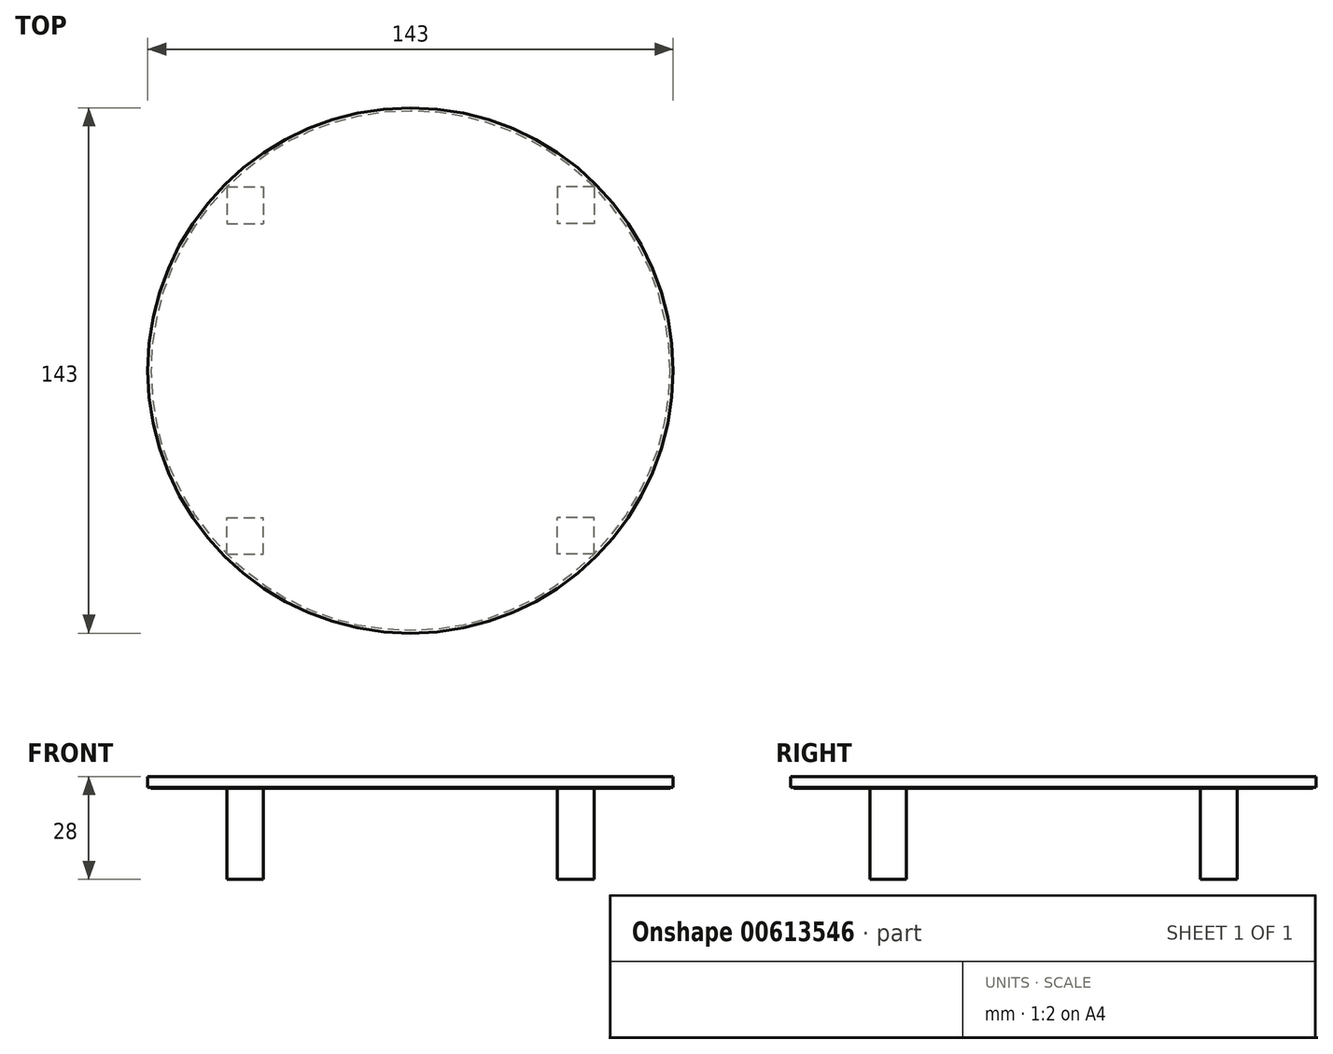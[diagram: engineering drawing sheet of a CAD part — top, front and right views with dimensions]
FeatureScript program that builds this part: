
annotation { "Feature Type Name" : "Feature", "Feature Type Description" : "" }
export const myFeature = defineFeature(function(context is Context, id is Id, definition is map)
    precondition{}
    {
        {
            var Q0;
            Q0=qCreatedBy(makeId("Top.planeOp"),FACE);
            var sketch = newSketch(context, id + "F0", { "sketchPlane" : qUnion([Q0])});
            skLineSegment(sketch, "E0.bottom", {"start": v(50, -50) * mm, "end": v(40, -50) * mm});
            skLineSegment(sketch, "E0.top", {"start": v(50, 50) * mm, "end": v(40, 50) * mm});
            skLineSegment(sketch, "E0.left", {"start": v(50, -50) * mm, "end": v(50, -40) * mm});
            skLineSegment(sketch, "E0.right", {"start": v(-50, -50) * mm, "end": v(-50, -40) * mm});
            skPoint(sketch, "E0.middle", {"position": v(0, 0) * mm});
            skLineSegment(sketch, "E1.bottom", {"start": v(-50, 50) * mm, "end": v(-40, 50) * mm});
            skLineSegment(sketch, "E1.top", {"start": v(-50, 40) * mm, "end": v(-40, 40) * mm});
            skLineSegment(sketch, "E1.left", {"start": v(-50, 50) * mm, "end": v(-50, 40) * mm});
            skLineSegment(sketch, "E1.right", {"start": v(-40, 50) * mm, "end": v(-40, 40) * mm});
            skLineSegment(sketch, "E2.top", {"start": v(50, 40) * mm, "end": v(40, 40) * mm});
            skLineSegment(sketch, "E2.left", {"start": v(50, 50) * mm, "end": v(50, 40) * mm});
            skLineSegment(sketch, "E2.right", {"start": v(40, 50) * mm, "end": v(40, 40) * mm});
            skLineSegment(sketch, "E3.top", {"start": v(50, -40) * mm, "end": v(40, -40) * mm});
            skLineSegment(sketch, "E3.right", {"start": v(40, -50) * mm, "end": v(40, -40) * mm});
            skLineSegment(sketch, "E4.bottom", {"start": v(-50, -50) * mm, "end": v(-40, -50) * mm});
            skLineSegment(sketch, "E4.top", {"start": v(-50, -40) * mm, "end": v(-40, -40) * mm});
            skLineSegment(sketch, "E4.right", {"start": v(-40, -50) * mm, "end": v(-40, -40) * mm});
            skLineSegment(sketch, "E5.trimOffspring", {"start": v(-40, 50) * mm, "end": v(-50, 50) * mm});
            skLineSegment(sketch, "E6.trimOffspring", {"start": v(50, 40) * mm, "end": v(50, 50) * mm});
            skLineSegment(sketch, "E7.trimOffspring", {"start": v(-40, -50) * mm, "end": v(-50, -50) * mm});
            skLineSegment(sketch, "E8.trimOffspring", {"start": v(-50, 40) * mm, "end": v(-50, 50) * mm});
            skSolve(sketch);
        }
        {
            var Q0;
            Q0 = qSketchRegion(id + "F0", true);
            extrude(context, id + "F1", {"entities" : qUnion([Q0]), "depth" : 25 * mm, "offsetDistance" : 25 * mm});
        }
        {
            var Q0;
            Q0=makeQuery(id+"F1.opExtrude","CAP_FACE",FACE,{"disambiguationData":[OSD([sQuery(id+"F0.wireOp",EDGE,"E1.top"),sQuery(id+"F0.wireOp",EDGE,"E1.right"),sQuery(id+"F0.wireOp",EDGE,"E5.trimOffspring"),sQuery(id+"F0.wireOp",EDGE,"E8.trimOffspring")])],"isStart":false});
            var sketch = newSketch(context, id + "F2", { "sketchPlane" : qUnion([Q0])});
            skCircle(sketch, "E9", {"center": v(0, 0) * mm, "radius": 71.5 * mm});
            skSolve(sketch);
        }
        {
            var Q0;
            Q0 = qSketchRegion(id + "F2", true);
            extrude(context, id + "F3", {"entities" : qUnion([Q0]), "depth" : 3 * mm, "offsetDistance" : 25 * mm});
        }
        {
            var Q0;
            Q0=makeQuery(id+"F3.opExtrude","CAP_FACE",FACE,{"disambiguationData":[OSD([sQuery(id+"F2.wireOp",EDGE,"E9")])],"isStart":false});
            var sketch = newSketch(context, id + "F4", { "sketchPlane" : qUnion([Q0])});
            skCircle(sketch, "E10", {"center": v(0, 0) * mm, "radius": 50 * mm});
            skSolve(sketch);
        }
        {
            var Q0;
            Q0=sQuery(id+"F4.wireOp",EDGE,"E10");
            extrude(context, id + "F5", {"bodyType" : ToolBodyType.SURFACE, "surfaceEntities" : qUnion([Q0]), "depth" : 0.2 * mm, "offsetDistance" : 25 * mm});
        }
        {
            var Q0;
            Q0=makeQuery(id+"F3.opExtrude","CAP_FACE",FACE,{"disambiguationData":[OSD([sQuery(id+"F2.wireOp",EDGE,"E9")])],"isStart":true});
            var sketch = newSketch(context, id + "F6", { "sketchPlane" : qUnion([Q0])});
            skCircle(sketch, "E11", {"center": v(0, 0) * mm, "radius": 70.63 * mm});
            skSolve(sketch);
        }
        {
            var Q0;
            Q0 = qSketchRegion(id + "F6", true);
            extrude(context, id + "F7", {"entities" : qUnion([Q0]), "depth" : .2 * mm, "offsetDistance" : 25 * mm});
        }
    });
